# Revit family: Drain_Floor-JayR.Smith-Round_Type-2030-2031_Series
name_source: partatom
category: Plumbing Fixtures
units: mm (PartAtom-declared; Revit-internal decimal feet)

## family parameters
Always vertical = No
Cut with Voids When Loaded = No
OmniClass Number = 23.70.50.21.24.11
OmniClass Title = Roof Waste Water Drains
Part Type = Normal
Room Calculation Point = No
Round Connector Dimension = Use Diameter
Shared = Yes
Work Plane-Based = Yes

## types (6) — shared parameters
Assembly Code = D2040200
B - Sediment Bucket = No
BB-Bronze Body = No
Ball Float Backwater Valve -BFV = No
CP - Chrome Plated Strainer = No
CW Connection = No
Default Elevation = 0"
Description = Floor Drains With Adjustable Strainer Heads and Varying Trap Options
Finish = Cast Iron-Jay R Smith-Duco Coated
Flange Diameter = 10 1/2"
G - Galvanized Cast Iron = No
H - Hinged Grate = No
HW Connection = No
High Auxiliary Inlet -NH = No
Installation Type = Roof
Load Rating = Light Duty having a Safe Live (Static) Load less than 2,000 lbs. (900 kg) per ASME A112.6.3 Floor Drain Standard
Low Auxiliary Inlet -NL = No
Manufacturer = Jay R. Smith
Material = Cast Iron-Jay R Smith-Duco Coated
NB - Nickel Bronze Strainer = No
PB - Polished Bronze Strainer = No
Product Documentation Link = https://www.jrsmith.com
Product Page URL = https://www.jrsmith.com
Trap Primer Connection -P050 = No
Type Comments = DEEP TRAP - SIDE OUTLET-ROUND TOP
U - Vandal Proof Screw = No
URL = http://www.jrsmith.com
Vent Connection = No
Waste Connection = Yes

## per-type parameters (varying)
| type | "G" if Threaded and "H" if Spigot | A | B | Connection Description | Connection Radius | Connection Size | D | Depth for F | Diameter | E | F | Height | MIN-X-MAX | MIN-X-MAX constraint | Pipe Curve Radius | Pipe Depth | Pipe Radius | Smaller Pipe Curve Edge | Smaller Pipe Length |
| 2030T02 | 5" | 2" | 5" | 2" Threaded Outlet Connection | 1" | 2" | 1 3/4" | 2 1/4" | 5" | 5 1/4" | 2" | 8 1/4" | 1 1/4" | 1 1/4" | 2" | 2 1/4" | 1" | 1" | 2 1/4" |
| 2030T03 | 8" | 3" | 6" | 3" Threaded Outlet Connection | 1 1/2" | 3" | 2" | 2 1/2" | 6" | 7" | 2 1/4" | 10 1/4" | 1 1/4" | 1 1/4" | 2" | 3 1/2" | 1 1/2" | 1 1/2" | 5 1/2" |
| 2030T04 | 10" | 4" | 8" | 4" Threaded Outlet Connection | 2" | 4" | 3" | 2 1/2" | 8" | 8 1/2" | 2 1/2" | 13" | 1 1/2" | 1 1/2" | 2 1/4" | 4 1/4" | 2" | 2" | 7 1/2" |
| 2031S02 | 8" | 2" | 5" | 2" Spigot Outlet Connection | 1" | 2" | 1 3/4" | 1 1/4" | 5" | 5 1/4" | 2" | 8 1/4" | 1 1/4" | 1 1/4" | 2" | 1 3/4" | 1 1/2" | 1" | 5 1/2" |
| 2031S03 | 10" | 3" | 6" | 3" Spigot Outlet Connection | 1 1/2" | 3" | 2" | 2 1/2" | 6" | 7" | 2 1/4" | 10 1/4" | 1 1/4" | 1 1/4" | 2" | 3 1/2" | 1 1/2" | 1 1/2" | 7 1/2" |
| 2031S04 | 12 3/4" | 4" | 8" | 4" Spigot Outlet Connection | 2" | 4" | 3" | 2 1/2" | 8" | 8 1/2" | 2 1/2" | 13" | 1 1/2" | 1 1/2" | 2 1/4" | 4 1/4" | 2" | 1" | 9 1/2" |

note: column(s) folded — value = type name in every type: Model

## geometry (parser evidence)
native form markers: Sweep x2
no freeform markers — native parametric forms only
